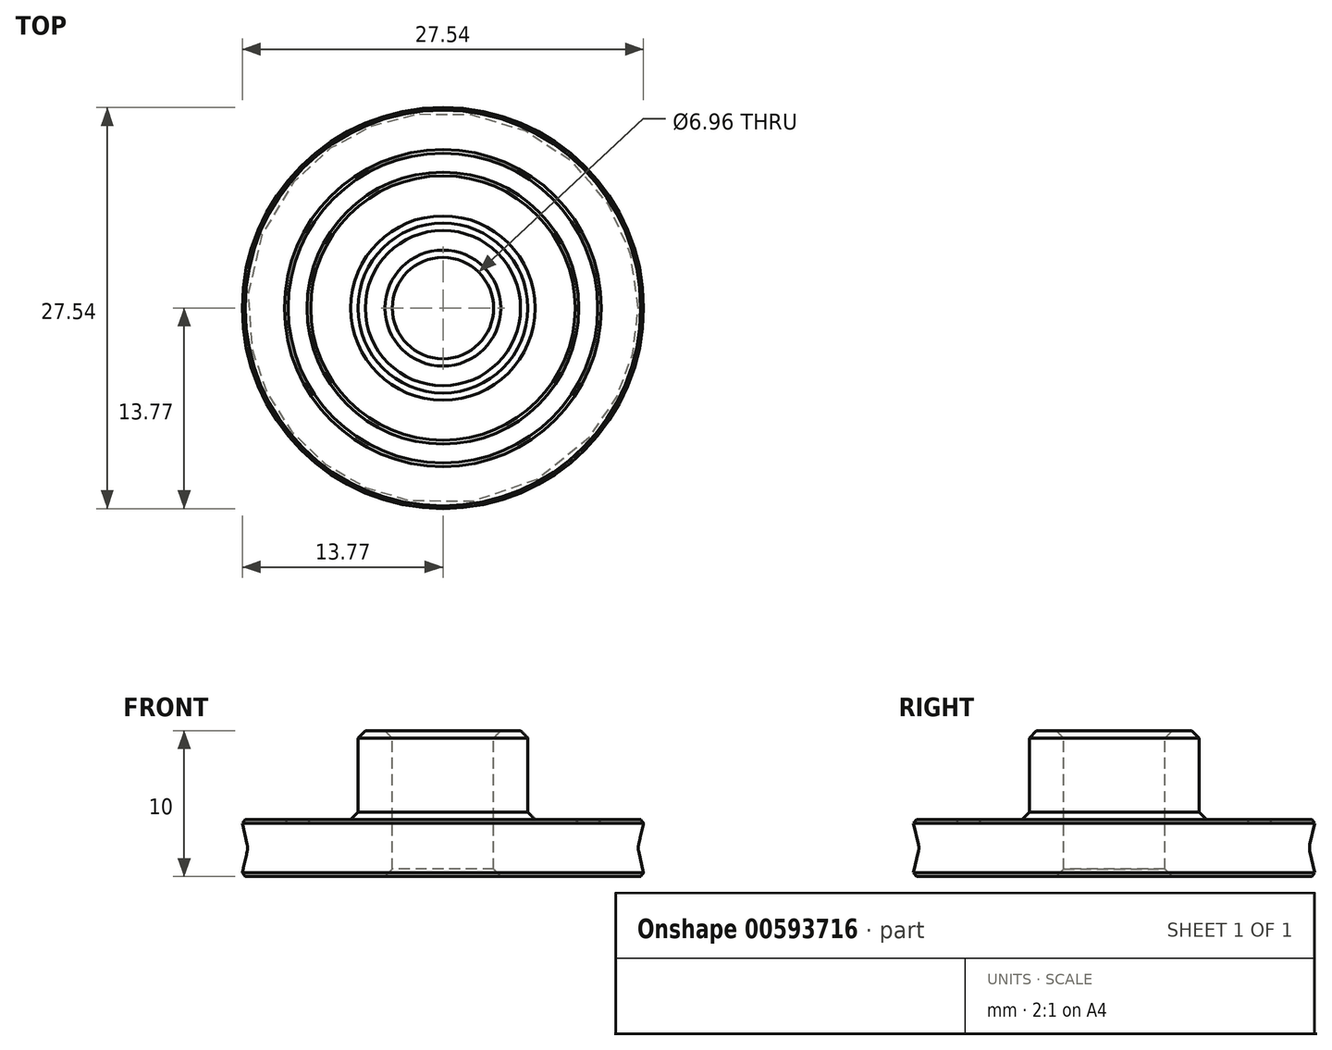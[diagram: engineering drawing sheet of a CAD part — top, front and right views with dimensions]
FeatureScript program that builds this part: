
annotation { "Feature Type Name" : "Feature", "Feature Type Description" : "" }
export const myFeature = defineFeature(function(context is Context, id is Id, definition is map)
    precondition{}
    {
        {
            var Q0;
            Q0=qCreatedBy(makeId("Front.planeOp"),FACE);
            var sketch = newSketch(context, id + "F0", { "sketchPlane" : qUnion([Q0])});
            skLineSegment(sketch, "E0.bottom", {"start": v(3.48, 10) * mm, "end": v(5.83, 10) * mm});
            skLineSegment(sketch, "E0.top", {"start": v(3.48, 0) * mm, "end": v(5.83, 0) * mm});
            skLineSegment(sketch, "E0.left", {"start": v(3.48, 10) * mm, "end": v(3.48, 0) * mm});
            skLineSegment(sketch, "E0.right", {"start": v(5.83, 10) * mm, "end": v(5.83, 3.9) * mm});
            skLineSegment(sketch, "E1.bottom", {"start": v(5.83, 0) * mm, "end": v(13.83, 0) * mm});
            skLineSegment(sketch, "E1.top", {"start": v(5.83, 3.9) * mm, "end": v(13.83, 3.9) * mm});
            skLineSegment(sketch, "E2", {"start": v(0, 27.12) * mm, "end": v(0, 0) * mm});
            skLineSegment(sketch, "E3", {"start": v(13.83, 0) * mm, "end": v(13.39, 1.95) * mm});
            skLineSegment(sketch, "E4", {"start": v(13.39, 1.95) * mm, "end": v(13.83, 3.9) * mm});
            skLineSegment(sketch, "E5", {"start": v(7.81, 3.9) * mm, "end": v(7.81, 0) * mm, "construction": true});
            skLineSegment(sketch, "E6", {"start": v(7.81, 1.95) * mm, "end": v(15.14, 1.95) * mm, "construction": true});
            skSolve(sketch);
        }
        {
            var Q0;
            Q0=makeQuery(id+"F0.imprint","IMPRINT",FACE,{"disambiguationData":[TD([[makeQuery(id+"F0.imprint","IMPRINT",EDGE,{"derivedFrom":sQuery(id+"F0.wireOp",EDGE,"E0.bottom")}),-1.0]])]});
            var Q1;
            Q1=sQuery(id+"F0.wireOp",EDGE,"E2");
            revolve(context, id + "F1", {"entities" : qUnion([Q0]), "axis" : qUnion([Q1]), "revolveType" : RevolveType.FULL});
        }
        {
            var Q0;
            Q0=makeQuery(id+"F1.opRevolve","SWEPT_EDGE",EDGE,{"disambiguationData":[OSD([sQuery(id+"F0.wireOp",EDGE,"E1.top"),sQuery(id+"F0.wireOp",EDGE,"E4")])]});
            var Q1;
            Q1=makeQuery(id+"F1.opRevolve","SWEPT_EDGE",EDGE,{"disambiguationData":[OSD([sQuery(id+"F0.wireOp",EDGE,"E1.bottom"),sQuery(id+"F0.wireOp",EDGE,"E3")])]});
            chamfer(context, id + "F2", {"entities" : qUnion([Q0, Q1]), "width" : .2 * mm, "tangentPropagation" : true});
        }
        {
            var Q0;
            Q0=makeQuery(id+"F1.opRevolve","SWEPT_EDGE",EDGE,{"disambiguationData":[OSD([sQuery(id+"F0.wireOp",EDGE,"E3"),sQuery(id+"F0.wireOp",EDGE,"E4")])]});
            fillet(context, id + "F3", {"entities" : qUnion([Q0]), "radius" : 1 * mm, "tangentPropagation" : true, "allowEdgeOverflow" : false});
        }
        {
            var Q0;
            Q0=makeQuery(id+"F1.opRevolve","SWEPT_EDGE",EDGE,{"disambiguationData":[OSD([sQuery(id+"F0.wireOp",EDGE,"E0.bottom"),sQuery(id+"F0.wireOp",EDGE,"E0.right")])]});
            var Q1;
            Q1=makeQuery(id+"F1.opRevolve","SWEPT_EDGE",EDGE,{"disambiguationData":[OSD([sQuery(id+"F0.wireOp",EDGE,"E0.bottom"),sQuery(id+"F0.wireOp",EDGE,"E0.left")])]});
            var Q2;
            Q2=makeQuery(id+"F1.opRevolve","SWEPT_EDGE",EDGE,{"disambiguationData":[OSD([sQuery(id+"F0.wireOp",EDGE,"E0.right"),sQuery(id+"F0.wireOp",EDGE,"E1.top")])]});
            chamfer(context, id + "F4", {"entities" : qUnion([Q0, Q1, Q2]), "width" : .5 * mm, "tangentPropagation" : true});
        }
        {
            var Q0;
            Q0=makeQuery(id+"F1.opRevolve","SWEPT_EDGE",EDGE,{"disambiguationData":[OSD([sQuery(id+"F0.wireOp",EDGE,"E0.top"),sQuery(id+"F0.wireOp",EDGE,"E0.left")])]});
            chamfer(context, id + "F5", {"entities" : qUnion([Q0]), "width" : 0.5 * mm, "tangentPropagation" : true});
        }
        {
            var Q0;
            Q0=makeQuery(id+"F1.opRevolve","SWEPT_FACE",FACE,{"disambiguationData":[OSD([sQuery(id+"F0.wireOp",EDGE,"E1.top")])]});
            var sketch = newSketch(context, id + "F6", { "sketchPlane" : qUnion([Q0])});
            skCircle(sketch, "E7.0", {"center": v(0, 0) * mm, "radius": 11.63 * mm});
            skCircle(sketch, "E8.0", {"center": v(0, 0) * mm, "radius": 8.33 * mm});
            skSolve(sketch);
        }
        {
            var Q0;
            Q0 = qSketchRegion(id + "F6", true);
            extrude(context, id + "F7", {"entities" : qUnion([Q0]), "operationType" : NewBodyOperationType.REMOVE, "oppositeDirection" : true, "depth" : .25 * mm, "offsetDistance" : 25 * mm});
        }
        {
            var Q0;
            Q0=makeQuery(id+"F7.boolean.opBoolean","COPY",FACE,{"derivedFrom":makeQuery(id+"F7.opExtrude","CAP_FACE",FACE,{"disambiguationData":[OSD([sQuery(id+"F6.wireOp",EDGE,"E7.0"),sQuery(id+"F6.wireOp",EDGE,"E8.0")])],"isStart":false})});
            chamfer(context, id + "F8", {"entities" : qUnion([Q0]), "width" : 1 * mm, "tangentPropagation" : true});
        }
    });
